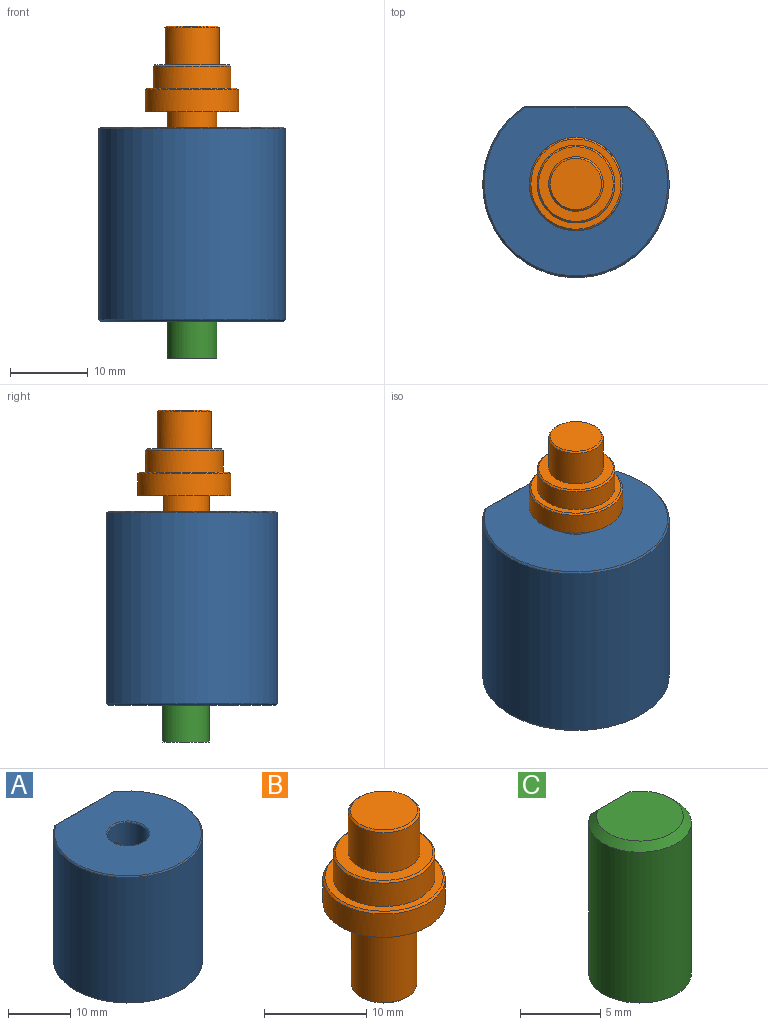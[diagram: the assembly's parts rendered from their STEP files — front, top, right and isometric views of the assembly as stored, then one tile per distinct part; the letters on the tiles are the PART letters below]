
ASSEMBLY  parts=3 mates=4
PART A: 13 faces, bbox 24x22x25 mm
  f0: plane 24.6x13.27mm, normal (0,1,0), area 312.2mm2, adj f2,f5,f6,f9,f12
  f1: cylinder r=3.25mm len=24.6mm, axis (0,0,-1), area 487.8mm2, adj f5,f6,f7,f10
  f2: cylinder r=12mm len=24.6mm, axis (0,0,-1), area 1509mm2, adj f0,f8,f11
  f3: plane 23.6x21.6mm, normal (0,0,1), area 382.2mm2, adj f10,f11,f12
  f4: plane 23.6x21.6mm, normal (0,0,-1), area 382.2mm2, adj f7,f8,f9
  f5: cylinder r=1.5mm len=7.12mm, axis (0,1,0), area 65.3mm2, adj f0,f1
  f6: cylinder r=1.5mm len=7.12mm, axis (0,1,0), area 65.3mm2, adj f0,f1
  f7: cone r=3.45mm half-angle=45deg, axis (0,0,-1), area 6mm2, adj f1,f4
  f8: cone r=12mm half-angle=45deg, axis (0,0,1), area 17.2mm2, adj f2,f4,f9
  f9: plane 13.27x0.2mm, normal (0,0.71,-0.71), area 3.7mm2, adj f0,f4,f8
  f10: cone r=3.25mm half-angle=45deg, axis (0,0,1), area 6mm2, adj f1,f3
  f11: cone r=11.8mm half-angle=45deg, axis (0,0,-1), area 17.2mm2, adj f2,f3,f12
  f12: plane 13.27x0.2mm, normal (0,0.71,0.71), area 3.7mm2, adj f0,f3,f11
PART B: 15 faces, bbox 12x12x21 mm
  f0: cylinder r=3.2mm len=9.8mm, axis (0,0,1), area 160.5mm2, adj f8,f9,f10
  f1: plane 6x5.47mm, normal (0,0,-1), area 27.1mm2, adj f10,f11
  f2: plane 6.6x6.6mm, normal (0,0,1), area 34.2mm2, adj f14
  f3: cylinder r=3.5mm len=7mm, axis (0,0,1), area 105.6mm2, adj f4,f14
  f4: plane 9.6x9.6mm, normal (0,0,1), area 33.9mm2, adj f3,f13
  f5: cylinder r=5mm len=10mm, axis (0,0,1), area 88mm2, adj f6,f13
  f6: plane 11.6x11.6mm, normal (0,0,1), area 27.1mm2, adj f5,f12
  f7: cylinder r=6mm len=12mm, axis (0,0,1), area 105.6mm2, adj f8,f12
  f8: plane 12x12mm, normal (0,0,-1), area 82.2mm2, adj f0,f7,f9
  f9: plane 9.8x3.52mm, normal (0,1,0), area 34.5mm2, adj f0,f8,f11
  f10: cone r=3.2mm half-angle=45deg, axis (0,0,1), area 4.5mm2, adj f0,f1,f11
  f11: plane 3.52x0.2mm, normal (0,0.71,-0.71), area 1mm2, adj f1,f9,f10
  f12: cone r=5.8mm half-angle=45deg, axis (0,0,-1), area 10.5mm2, adj f6,f7
  f13: cone r=4.8mm half-angle=45deg, axis (0,0,-1), area 8.7mm2, adj f4,f5
  f14: cone r=3.3mm half-angle=45deg, axis (0,0,-1), area 6mm2, adj f2,f3
PART C: 6 faces, bbox 6.4x6x12 mm
  f0: plane 11.5x3.1mm, normal (0,1,0), area 35.6mm2, adj f1,f3,f5
  f1: cylinder r=3.2mm len=11.5mm, axis (0,0,-1), area 194mm2, adj f0,f3,f4
  f2: plane 5.4x5mm, normal (0,0,1), area 22.1mm2, adj f4,f5
  f3: plane 6.4x6mm, normal (0,0,-1), area 31.3mm2, adj f0,f1
  f4: cone r=2.7mm half-angle=45deg, axis (0,0,-1), area 10.9mm2, adj f1,f2,f5
  f5: plane 3.11x0.51mm, normal (0,0.71,0.71), area 2.1mm2, adj f0,f2,f4
PLACE A t=(10.35,10.47,-2.54)mm
PLACE B t=(10.35,10.47,14.46)mm
PLACE C t=(10.35,10.47,-7.25)mm fixed
MATE cylindrical B.f0 <-> C.f1  axis (0,0,1) through (10.35,10.47,14.66)mm
MATE parallel A.f0 <-> C.f0  axis (0,1,0) through (10.35,20.47,9.96)mm
MATE parallel B.f9 <-> A.f0  axis (0,1,0) through (10.35,13.15,19.56)mm
MATE cylindrical C.f1 <-> A.f1  axis (0,0,-1) through (10.35,10.47,-7.25)mm
